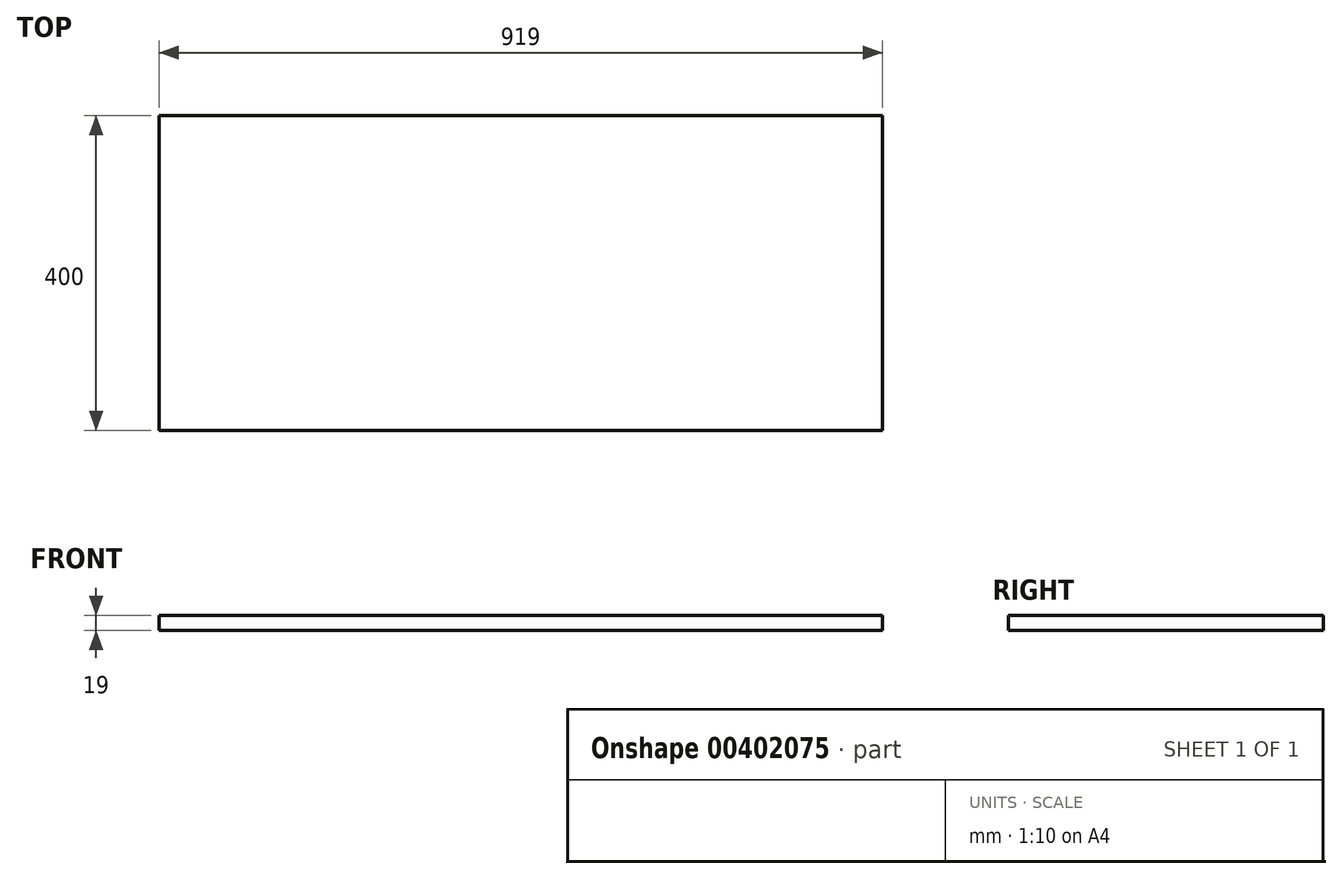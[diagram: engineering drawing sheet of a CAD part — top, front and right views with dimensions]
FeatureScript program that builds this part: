
annotation { "Feature Type Name" : "Feature", "Feature Type Description" : "" }
export const myFeature = defineFeature(function(context is Context, id is Id, definition is map)
    precondition{}
    {
        {
            var Q0;
            Q0=qCreatedBy(makeId("Top.planeOp"),FACE);
            var sketch = newSketch(context, id + "F0", { "sketchPlane" : qUnion([Q0])});
            skLineSegment(sketch, "E0.bottom", {"start": v(0, 0) * mm, "end": v(919, 0) * mm});
            skLineSegment(sketch, "E0.top", {"start": v(0, 400) * mm, "end": v(919, 400) * mm});
            skLineSegment(sketch, "E0.left", {"start": v(0, 0) * mm, "end": v(0, 400) * mm});
            skLineSegment(sketch, "E0.right", {"start": v(919, 0) * mm, "end": v(919, 400) * mm});
            skSolve(sketch);
        }
        {
            var Q0;
            Q0 = qSketchRegion(id + "F0", true);
            extrude(context, id + "F1", {"entities" : qUnion([Q0]), "depth" : 19 * mm});
        }
    });
